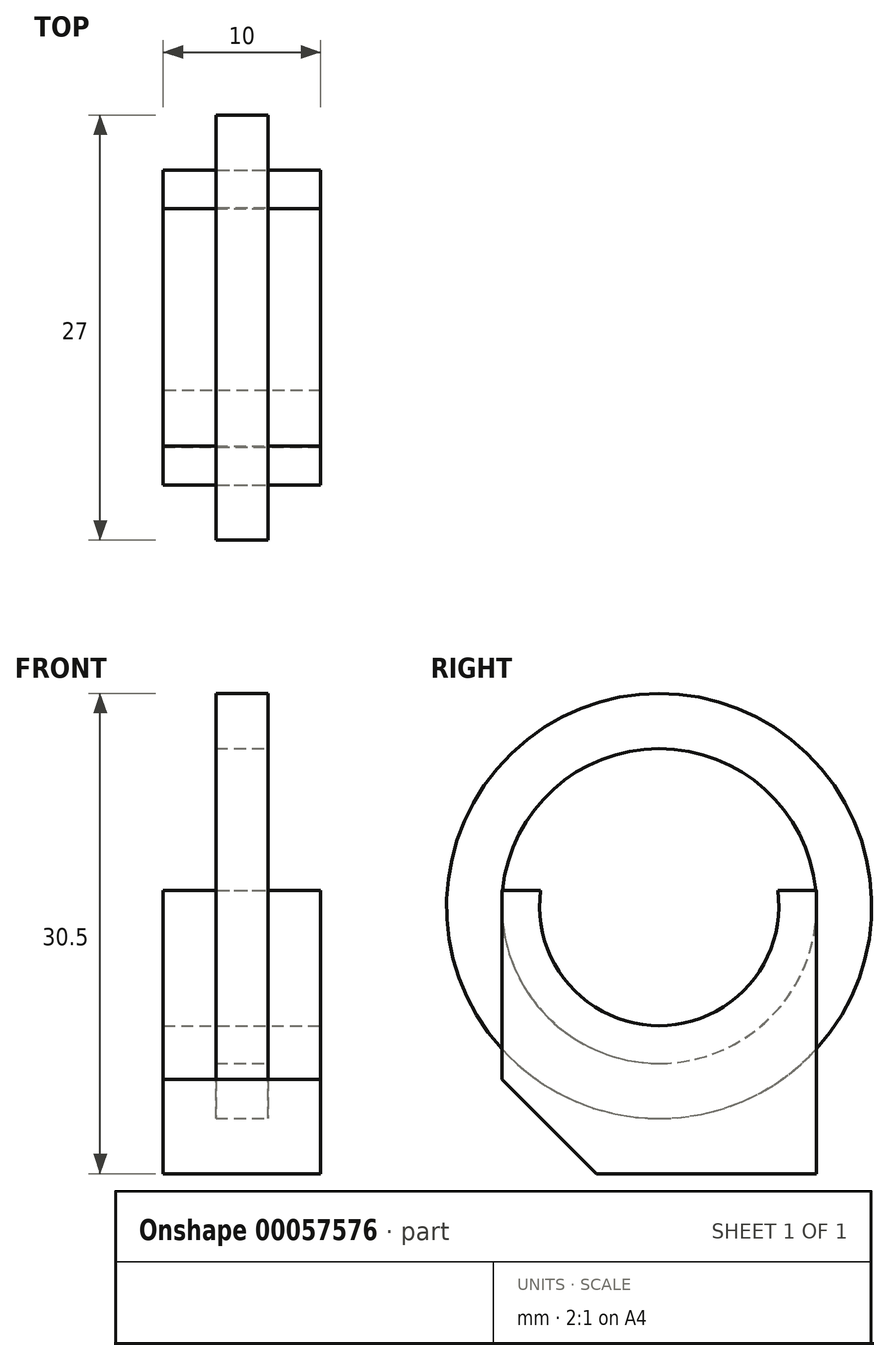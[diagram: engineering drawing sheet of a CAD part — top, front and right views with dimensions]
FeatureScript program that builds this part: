
annotation { "Feature Type Name" : "Feature", "Feature Type Description" : "" }
export const myFeature = defineFeature(function(context is Context, id is Id, definition is map)
    precondition{}
    {
        {
            var Q0;
            Q0=qCreatedBy(makeId("Top.planeOp"),FACE);
            var sketch = newSketch(context, id + "F0", { "sketchPlane" : qUnion([Q0])});
            skLineSegment(sketch, "E0.bottom", {"start": v(0, 0) * mm, "end": v(10, 0) * mm});
            skLineSegment(sketch, "E0.top", {"start": v(0, 20) * mm, "end": v(10, 20) * mm});
            skLineSegment(sketch, "E0.left", {"start": v(0, 0) * mm, "end": v(0, 20) * mm});
            skLineSegment(sketch, "E0.right", {"start": v(10, 0) * mm, "end": v(10, 20) * mm});
            skSolve(sketch);
        }
        {
            var Q0;
            Q0=makeQuery(id+"F0.imprint","IMPRINT",FACE,{"disambiguationData":[TD([[makeQuery(id+"F0.imprint","IMPRINT",EDGE,{"derivedFrom":sQuery(id+"F0.wireOp",EDGE,"E0.bottom")}),1.0]])]});
            extrude(context, id + "F1", {"entities" : qUnion([Q0]), "depth" : 18 * mm});
        }
        {
            var Q0;
            Q0=makeQuery(id+"F1.opExtrude","SWEPT_FACE",FACE,{"disambiguationData":[OSD([sQuery(id+"F0.wireOp",EDGE,"E0.right")])]});
            var sketch = newSketch(context, id + "F2", { "sketchPlane" : qUnion([Q0])});
            skCircle(sketch, "E1", {"center": v(10, 17) * mm, "radius": 7.6 * mm});
            skPoint(sketch, "E1.centerSnap0", {"position": v(10, 18) * mm});
            skSolve(sketch);
        }
        {
            var Q0;
            Q0=qSketchRegion(id+"F2",true);
            extrude(context, id + "F3", {"entities" : qUnion([Q0]), "operationType" : NewBodyOperationType.REMOVE, "endBound" : BoundingType.THROUGH_ALL, "oppositeDirection" : true, "depth" : 25 * mm});
        }
        {
            var Q0;
            Q0=makeQuery(id+"F1.opExtrude","SWEPT_FACE",FACE,{"disambiguationData":[OSD([sQuery(id+"F0.wireOp",EDGE,"E0.right")])]});
            var Q1;
            Q1=makeQuery(id+"F1.opExtrude","SWEPT_FACE",FACE,{"disambiguationData":[OSD([sQuery(id+"F0.wireOp",EDGE,"E0.left")])]});
            cPlane(context, id + "F4", {"entities" : qUnion([Q0, Q1]), "cplaneType" : CPlaneType.MID_PLANE, "offset" : 150 * mm, "width" : 150 * mm, "height" : 150 * mm});
        }
        {
            var Q0;
            Q0=qCreatedBy(id+"F4.planeOp",FACE);
            var sketch = newSketch(context, id + "F5", { "sketchPlane" : qUnion([Q0])});
            skArc(sketch, "E2.0", {"start": v(2.47, 18) * mm, "mid": v(10, 9.4) * mm, "end": v(17.53, 18) * mm});
            skCircle(sketch, "E3", {"center": v(10, 17) * mm, "radius": 10 * mm});
            skCircle(sketch, "E4.0", {"center": v(10, 17) * mm, "radius": 13.5 * mm});
            skSolve(sketch);
        }
        {
            var Q0;
            Q0=makeQuery(id+"F5.imprint","IMPRINT",FACE,{"disambiguationData":[TD([[makeQuery(id+"F5.imprint","IMPRINT",EDGE,{"derivedFrom":sQuery(id+"F5.wireOp",EDGE,"E3")}),-1.0]])]});
            extrude(context, id + "F6", {"entities" : qUnion([Q0]), "endBound" : BoundingType.SYMMETRIC, "oppositeDirection" : true, "depth" : 3.3 * mm});
        }
        {
            var Q0;
            Q0=makeQuery(id+"F1.opExtrude","CAP_EDGE",EDGE,{"disambiguationData":[OSD([sQuery(id+"F0.wireOp",EDGE,"E0.bottom")])],"isStart":true});
            chamfer(context, id + "F7", {"entities" : qUnion([Q0]), "width" : 6 * mm, "tangentPropagation" : true});
        }
    });
